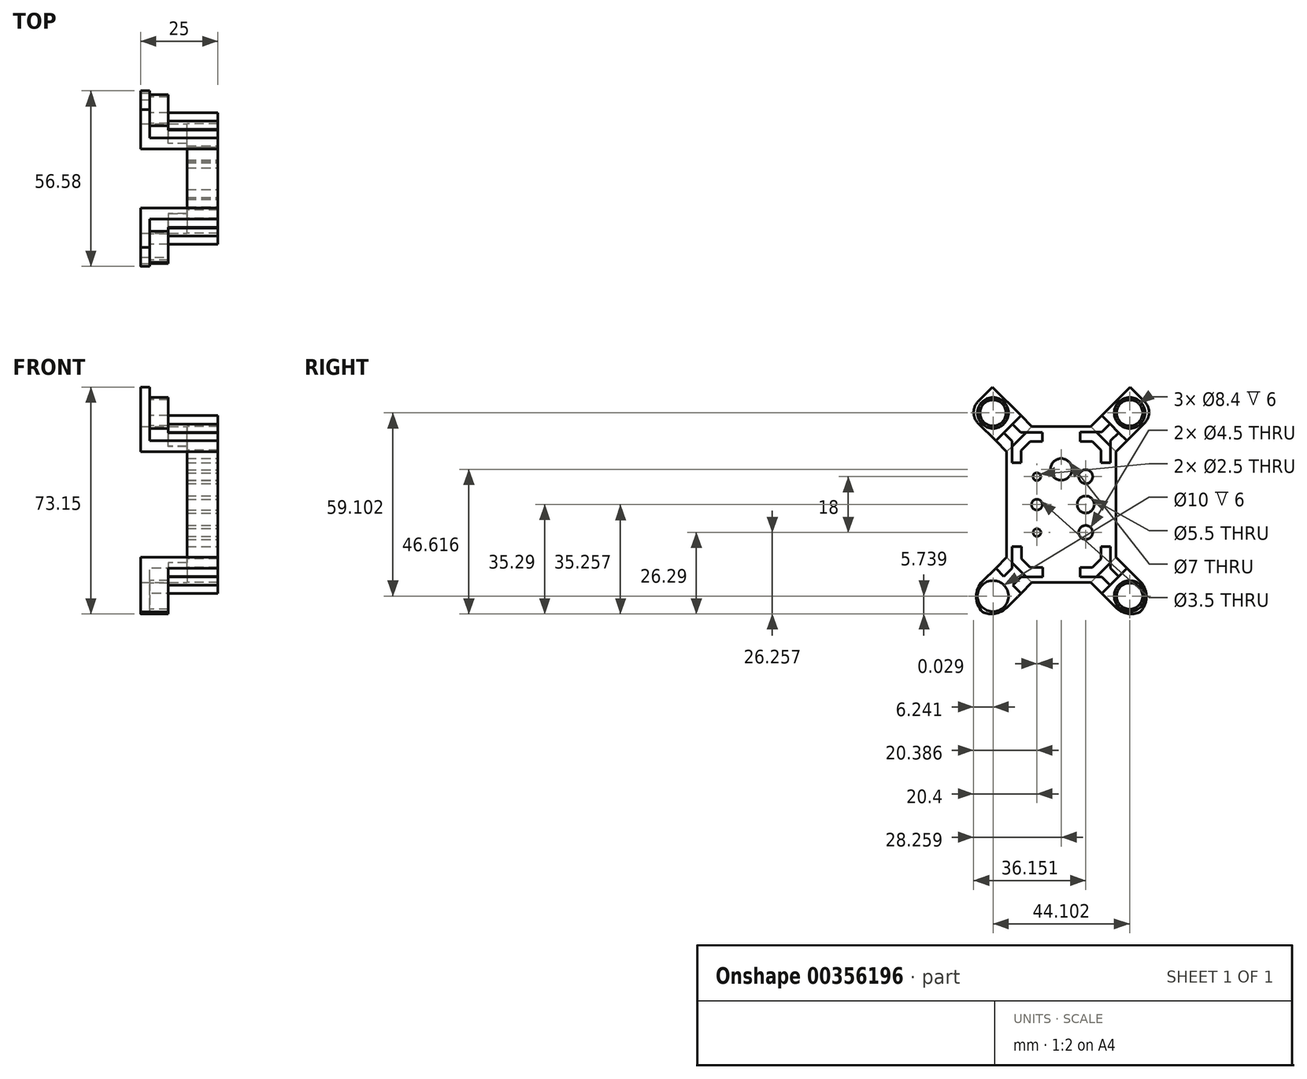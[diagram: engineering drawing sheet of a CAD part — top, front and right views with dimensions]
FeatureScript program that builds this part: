
annotation { "Feature Type Name" : "Feature", "Feature Type Description" : "" }
export const myFeature = defineFeature(function(context is Context, id is Id, definition is map)
    precondition{}
    {
        {
            var Q0;
            Q0=qCreatedBy(makeId("Right.planeOp"),FACE);
            var sketch = newSketch(context, id + "F0", { "sketchPlane" : qUnion([Q0])});
            skPoint(sketch, "E0", {"position": v(0, 42) * mm});
            skPoint(sketch, "E1", {"position": v(8.13, 50.13) * mm});
            skPoint(sketch, "E2", {"position": v(27.13, 50.13) * mm});
            skPoint(sketch, "E3", {"position": v(35.26, 42) * mm});
            skPoint(sketch, "E4", {"position": v(35.26, 8) * mm});
            skPoint(sketch, "E5", {"position": v(27.13, -0.13) * mm});
            skPoint(sketch, "E6", {"position": v(8.13, -0.13) * mm});
            skPoint(sketch, "E7", {"position": v(0, 8) * mm});
            skLineSegment(sketch, "E8", {"start": v(0, 42) * mm, "end": v(8.13, 50.13) * mm});
            skLineSegment(sketch, "E9", {"start": v(27.13, 50.13) * mm, "end": v(8.13, 50.13) * mm});
            skLineSegment(sketch, "E10", {"start": v(27.13, 50.13) * mm, "end": v(35.26, 42) * mm});
            skLineSegment(sketch, "E11", {"start": v(35.26, 8) * mm, "end": v(35.26, 42) * mm});
            skLineSegment(sketch, "E12", {"start": v(35.26, 8) * mm, "end": v(27.13, -0.13) * mm});
            skLineSegment(sketch, "E13", {"start": v(0, 8) * mm, "end": v(8.13, -0.13) * mm});
            skLineSegment(sketch, "E14", {"start": v(8.13, -0.13) * mm, "end": v(27.13, -0.13) * mm});
            skLineSegment(sketch, "E15", {"start": v(0, 8) * mm, "end": v(0, 42) * mm});
            skPoint(sketch, "E16", {"position": v(4.07, 46.07) * mm});
            skPoint(sketch, "E17", {"position": v(5.48, 47.48) * mm});
            skPoint(sketch, "E18", {"position": v(2.65, 44.65) * mm});
            skLineSegment(sketch, "E19", {"start": v(2.65, 44.65) * mm, "end": v(5, 42.3) * mm});
            skLineSegment(sketch, "E20", {"start": v(5.48, 47.48) * mm, "end": v(7.83, 45.13) * mm});
            skLineSegment(sketch, "E21", {"start": v(5.48, 47.48) * mm, "end": v(2.65, 44.65) * mm});
            skPoint(sketch, "E22", {"position": v(31.2, 46.07) * mm});
            skPoint(sketch, "E23", {"position": v(29.78, 47.48) * mm});
            skPoint(sketch, "E24", {"position": v(32.61, 44.65) * mm});
            skPoint(sketch, "E25", {"position": v(31.2, 3.93) * mm});
            skPoint(sketch, "E26", {"position": v(32.61, 5.35) * mm});
            skPoint(sketch, "E27", {"position": v(29.78, 2.52) * mm});
            skPoint(sketch, "E28", {"position": v(4.07, 3.93) * mm});
            skPoint(sketch, "E29", {"position": v(2.65, 5.35) * mm});
            skPoint(sketch, "E30", {"position": v(5.48, 2.52) * mm});
            skLineSegment(sketch, "E31", {"start": v(29.78, 47.48) * mm, "end": v(27.44, 45.13) * mm});
            skLineSegment(sketch, "E32", {"start": v(32.61, 44.65) * mm, "end": v(30.26, 42.3) * mm});
            skLineSegment(sketch, "E33", {"start": v(29.78, 2.52) * mm, "end": v(27.44, 4.87) * mm});
            skLineSegment(sketch, "E34", {"start": v(32.61, 5.35) * mm, "end": v(30.26, 7.7) * mm});
            skPoint(sketch, "E35", {"position": v(17.63, 50.13) * mm});
            skPoint(sketch, "E36", {"position": v(35.26, 25) * mm});
            skSolve(sketch);
        }
        {
            var Q0;
            {var subQ6=sQuery(id+"F0.wireOp",EDGE,"E9");Q0=makeQuery(id+"F0.imprint","IMPRINT",FACE,{"disambiguationData":[TD([[makeQuery(id+"F0.imprint","IMPRINT",EDGE,{"derivedFrom":subQ6}),1.0]])]});}
            extrude(context, id + "F1", {"entities" : qUnion([Q0]), "depth" : 10 * mm});
        }
        {
            var Q0;
            Q0=makeQuery(id+"F1.opExtrude","SWEPT_FACE",FACE,{"disambiguationData":[OSD([sQuery(id+"F0.wireOp",EDGE,"E12")])]});
            var sketch = newSketch(context, id + "F2", { "sketchPlane" : qUnion([Q0])});
            skPoint(sketch, "E37.oppositeSnap0", {"position": v(-5, 30.6) * mm});
            skLineSegment(sketch, "E37.bottom", {"start": v(-10, 19.1) * mm, "end": v(15, 19.1) * mm});
            skLineSegment(sketch, "E37.top", {"start": v(-10, 30.6) * mm, "end": v(15, 30.6) * mm});
            skLineSegment(sketch, "E37.left", {"start": v(-10, 19.1) * mm, "end": v(-10, 30.6) * mm});
            skLineSegment(sketch, "E37.right", {"start": v(15, 19.1) * mm, "end": v(15, 30.6) * mm});
            skSolve(sketch);
        }
        {
            var Q0;
            Q0 = qSketchRegion(id + "F2", true);
            extrude(context, id + "F3", {"entities" : qUnion([Q0]), "operationType" : NewBodyOperationType.ADD, "depth" : 5 * mm});
        }
        {
            var Q0;
            Q0=makeQuery(id+"F1.opExtrude","SWEPT_FACE",FACE,{"disambiguationData":[OSD([sQuery(id+"F0.wireOp",EDGE,"E10")])]});
            var sketch = newSketch(context, id + "F4", { "sketchPlane" : qUnion([Q0])});
            skLineSegment(sketch, "E38.bottom", {"start": v(-10, 4.76) * mm, "end": v(15, 4.76) * mm});
            skLineSegment(sketch, "E38.top", {"start": v(-10, 16.26) * mm, "end": v(15, 16.26) * mm});
            skLineSegment(sketch, "E38.left", {"start": v(-10, 4.76) * mm, "end": v(-10, 16.26) * mm});
            skLineSegment(sketch, "E38.right", {"start": v(15, 4.76) * mm, "end": v(15, 16.26) * mm});
            skSolve(sketch);
        }
        {
            var Q0;
            Q0 = qSketchRegion(id + "F4", true);
            extrude(context, id + "F5", {"entities" : qUnion([Q0]), "operationType" : NewBodyOperationType.ADD, "depth" : 5 * mm});
        }
        {
            var Q0;
            Q0=makeQuery(id+"F1.opExtrude","SWEPT_FACE",FACE,{"disambiguationData":[OSD([sQuery(id+"F0.wireOp",EDGE,"E13")])]});
            var sketch = newSketch(context, id + "F6", { "sketchPlane" : qUnion([Q0])});
            skPoint(sketch, "E39.oppositeSnap0", {"position": v(5, -5.84) * mm});
            skLineSegment(sketch, "E39.bottom", {"start": v(10, 5.66) * mm, "end": v(-15, 5.66) * mm});
            skLineSegment(sketch, "E39.top", {"start": v(10, -5.84) * mm, "end": v(-15, -5.84) * mm});
            skLineSegment(sketch, "E39.left", {"start": v(10, 5.66) * mm, "end": v(10, -5.84) * mm});
            skLineSegment(sketch, "E39.right", {"start": v(-15, 5.66) * mm, "end": v(-15, -5.84) * mm});
            skSolve(sketch);
        }
        {
            var Q0;
            Q0 = qSketchRegion(id + "F6", true);
            extrude(context, id + "F7", {"entities" : qUnion([Q0]), "operationType" : NewBodyOperationType.ADD, "depth" : 5 * mm});
        }
        {
            var Q0;
            Q0=makeQuery(id+"F1.opExtrude","SWEPT_FACE",FACE,{"disambiguationData":[OSD([sQuery(id+"F0.wireOp",EDGE,"E8")])]});
            var sketch = newSketch(context, id + "F8", { "sketchPlane" : qUnion([Q0])});
            skPoint(sketch, "E40.oppositeSnap0", {"position": v(5, 29.7) * mm});
            skLineSegment(sketch, "E40.bottom", {"start": v(10, 41.2) * mm, "end": v(-15, 41.2) * mm});
            skLineSegment(sketch, "E40.top", {"start": v(10, 29.7) * mm, "end": v(-15, 29.7) * mm});
            skLineSegment(sketch, "E40.left", {"start": v(10, 41.2) * mm, "end": v(10, 29.7) * mm});
            skLineSegment(sketch, "E40.right", {"start": v(-15, 41.2) * mm, "end": v(-15, 29.7) * mm});
            skSolve(sketch);
        }
        {
            var Q0;
            Q0 = qSketchRegion(id + "F8", true);
            extrude(context, id + "F9", {"entities" : qUnion([Q0]), "operationType" : NewBodyOperationType.ADD, "depth" : 5 * mm});
        }
        {
            var Q0;
            Q0=makeQuery(id+"F9.opExtrude","CAP_FACE",FACE,{"disambiguationData":[OSD([sQuery(id+"F8.wireOp",EDGE,"E40.bottom"),sQuery(id+"F8.wireOp",EDGE,"E40.top"),sQuery(id+"F8.wireOp",EDGE,"E40.left"),sQuery(id+"F8.wireOp",EDGE,"E40.right")])],"isStart":false});
            var sketch = newSketch(context, id + "F10", { "sketchPlane" : qUnion([Q0])});
            skPoint(sketch, "E41", {"position": v(10, 41.2) * mm});
            skPoint(sketch, "E42", {"position": v(10, 29.7) * mm});
            skPoint(sketch, "E43", {"position": v(10, 37.36) * mm});
            skPoint(sketch, "E44", {"position": v(10, 33.36) * mm});
            skLineSegment(sketch, "E45.bottom", {"start": v(10, 37.36) * mm, "end": v(-6, 37.36) * mm});
            skLineSegment(sketch, "E45.top", {"start": v(10, 33.36) * mm, "end": v(-6, 33.36) * mm});
            skLineSegment(sketch, "E45.left", {"start": v(10, 37.36) * mm, "end": v(10, 33.36) * mm});
            skLineSegment(sketch, "E45.right", {"start": v(-6, 37.36) * mm, "end": v(-6, 33.36) * mm});
            skSolve(sketch);
        }
        {
            var Q0;
            Q0 = qSketchRegion(id + "F10", true);
            extrude(context, id + "F11", {"entities" : qUnion([Q0]), "operationType" : NewBodyOperationType.REMOVE, "oppositeDirection" : true, "depth" : 8 * mm});
        }
        {
            var Q0;
            Q0=makeQuery(id+"F9.boolean.opBoolean","MERGE",FACE,{"derivedFrom":[makeQuery(id+"F7.boolean.opBoolean","MERGE",FACE,{"derivedFrom":[makeQuery(id+"F5.boolean.opBoolean","MERGE",FACE,{"derivedFrom":[makeQuery(id+"F3.boolean.opBoolean","MERGE",FACE,{"derivedFrom":[makeQuery(id+"F1.opExtrude","CAP_FACE",FACE,{"disambiguationData":[OSD([sQuery(id+"F0.wireOp",EDGE,"E8"),sQuery(id+"F0.wireOp",EDGE,"E9"),sQuery(id+"F0.wireOp",EDGE,"E10"),sQuery(id+"F0.wireOp",EDGE,"E11"),sQuery(id+"F0.wireOp",EDGE,"E12"),sQuery(id+"F0.wireOp",EDGE,"E13"),sQuery(id+"F0.wireOp",EDGE,"E14"),sQuery(id+"F0.wireOp",EDGE,"E15")])],"isStart":false}),makeQuery(id+"F3.opExtrude","SWEPT_FACE",FACE,{"disambiguationData":[OSD([sQuery(id+"F2.wireOp",EDGE,"E37.left")])]})]}),makeQuery(id+"F5.opExtrude","SWEPT_FACE",FACE,{"disambiguationData":[OSD([sQuery(id+"F4.wireOp",EDGE,"E38.left")])]})]}),makeQuery(id+"F7.opExtrude","SWEPT_FACE",FACE,{"disambiguationData":[OSD([sQuery(id+"F6.wireOp",EDGE,"E39.left")])]})]}),makeQuery(id+"F9.opExtrude","SWEPT_FACE",FACE,{"disambiguationData":[OSD([sQuery(id+"F8.wireOp",EDGE,"E40.left")])]})]});
            var sketch = newSketch(context, id + "F12", { "sketchPlane" : qUnion([Q0])});
            skLineSegment(sketch, "E46", {"start": v(4.7, 42.46) * mm, "end": v(4.7, 38.46) * mm});
            skLineSegment(sketch, "E47", {"start": v(4.7, 38.46) * mm, "end": v(1.7, 38.46) * mm});
            skLineSegment(sketch, "E48", {"start": v(1.7, 38.46) * mm, "end": v(1.7, 45.46) * mm});
            skLineSegment(sketch, "E49", {"start": v(7.54, 45.3) * mm, "end": v(11.54, 45.3) * mm});
            skLineSegment(sketch, "E50", {"start": v(11.54, 45.3) * mm, "end": v(11.54, 48.3) * mm});
            skLineSegment(sketch, "E51", {"start": v(11.54, 48.3) * mm, "end": v(4.54, 48.3) * mm});
            skSolve(sketch);
        }
        {
            var Q0;
            Q0=makeQuery(id+"F9.opExtrude","CAP_FACE",FACE,{"disambiguationData":[OSD([sQuery(id+"F8.wireOp",EDGE,"E40.bottom"),sQuery(id+"F8.wireOp",EDGE,"E40.top"),sQuery(id+"F8.wireOp",EDGE,"E40.left"),sQuery(id+"F8.wireOp",EDGE,"E40.right")])],"isStart":true});
            var sketch = newSketch(context, id + "F13", { "sketchPlane" : qUnion([Q0])});
            skLineSegment(sketch, "E52.bottom", {"start": v(0, 29.7) * mm, "end": v(15, 29.7) * mm});
            skLineSegment(sketch, "E52.top", {"start": v(0, 41.2) * mm, "end": v(15, 41.2) * mm});
            skLineSegment(sketch, "E52.left", {"start": v(0, 29.7) * mm, "end": v(0, 41.2) * mm});
            skLineSegment(sketch, "E52.right", {"start": v(15, 29.7) * mm, "end": v(15, 41.2) * mm});
            skSolve(sketch);
        }
        {
            var Q0;
            Q0 = qSketchRegion(id + "F13", true);
            extrude(context, id + "F14", {"entities" : qUnion([Q0]), "operationType" : NewBodyOperationType.ADD, "depth" : 7 * mm});
        }
        {
            var Q0;
            Q0 = qSketchRegion(id + "F12", true);
            var Q1;
            {var subQ0=sQuery(id+"F12.wireOp",EDGE,"E49");Q1=makeQuery(id+"F12.imprint","IMPRINT",FACE,{"disambiguationData":[TD([[makeQuery(id+"F12.imprint","IMPRINT",EDGE,{"derivedFrom":subQ0}),1.0]])]});}
            var Q2;
            {var subQ0=sQuery(id+"F12.wireOp",EDGE,"E46");Q2=makeQuery(id+"F12.imprint","IMPRINT",FACE,{"disambiguationData":[TD([[makeQuery(id+"F12.imprint","IMPRINT",EDGE,{"derivedFrom":subQ0}),-1.0]])]});}
            extrude(context, id + "F15", {"entities" : qUnion([Q0, Q1, Q2]), "operationType" : NewBodyOperationType.REMOVE, "oppositeDirection" : true, "depth" : 10 * mm});
        }
        {
            var Q0;
            Q0=makeQuery(id+"F5.opExtrude","CAP_FACE",FACE,{"disambiguationData":[OSD([sQuery(id+"F4.wireOp",EDGE,"E38.bottom"),sQuery(id+"F4.wireOp",EDGE,"E38.top"),sQuery(id+"F4.wireOp",EDGE,"E38.left"),sQuery(id+"F4.wireOp",EDGE,"E38.right")])],"isStart":false});
            var sketch = newSketch(context, id + "F16", { "sketchPlane" : qUnion([Q0])});
            skPoint(sketch, "E53", {"position": v(-10, 8.51) * mm});
            skPoint(sketch, "E54", {"position": v(-10, 12.51) * mm});
            skLineSegment(sketch, "E55.bottom", {"start": v(-10, 8.51) * mm, "end": v(6, 8.51) * mm});
            skLineSegment(sketch, "E55.top", {"start": v(-10, 12.51) * mm, "end": v(6, 12.51) * mm});
            skLineSegment(sketch, "E55.left", {"start": v(-10, 8.51) * mm, "end": v(-10, 12.51) * mm});
            skLineSegment(sketch, "E55.right", {"start": v(6, 8.51) * mm, "end": v(6, 12.51) * mm});
            skPoint(sketch, "E56", {"position": v(-10, 4.76) * mm});
            skPoint(sketch, "E57", {"position": v(-10, 16.26) * mm});
            skSolve(sketch);
        }
        {
            var Q0;
            Q0 = qSketchRegion(id + "F16", true);
            extrude(context, id + "F17", {"entities" : qUnion([Q0]), "operationType" : NewBodyOperationType.REMOVE, "oppositeDirection" : true, "depth" : 8 * mm});
        }
        {
            var Q0;
            Q0=makeQuery(id+"F5.opExtrude","CAP_FACE",FACE,{"disambiguationData":[OSD([sQuery(id+"F4.wireOp",EDGE,"E38.bottom"),sQuery(id+"F4.wireOp",EDGE,"E38.top"),sQuery(id+"F4.wireOp",EDGE,"E38.left"),sQuery(id+"F4.wireOp",EDGE,"E38.right")])],"isStart":true});
            var sketch = newSketch(context, id + "F18", { "sketchPlane" : qUnion([Q0])});
            skLineSegment(sketch, "E58.bottom", {"start": v(0, 16.26) * mm, "end": v(-15, 16.26) * mm});
            skLineSegment(sketch, "E58.top", {"start": v(0, 4.76) * mm, "end": v(-15, 4.76) * mm});
            skLineSegment(sketch, "E58.left", {"start": v(0, 16.26) * mm, "end": v(0, 4.76) * mm});
            skLineSegment(sketch, "E58.right", {"start": v(-15, 16.26) * mm, "end": v(-15, 4.76) * mm});
            skSolve(sketch);
        }
        {
            var Q0;
            Q0 = qSketchRegion(id + "F18", true);
            extrude(context, id + "F19", {"entities" : qUnion([Q0]), "operationType" : NewBodyOperationType.ADD, "depth" : 7 * mm});
        }
        {
            var Q0;
            Q0=makeQuery(id+"F3.opExtrude","CAP_FACE",FACE,{"disambiguationData":[OSD([sQuery(id+"F2.wireOp",EDGE,"E37.bottom"),sQuery(id+"F2.wireOp",EDGE,"E37.top"),sQuery(id+"F2.wireOp",EDGE,"E37.left"),sQuery(id+"F2.wireOp",EDGE,"E37.right")])],"isStart":false});
            var sketch = newSketch(context, id + "F20", { "sketchPlane" : qUnion([Q0])});
            skPoint(sketch, "E59", {"position": v(-10, 22.84) * mm});
            skPoint(sketch, "E60", {"position": v(-10, 26.84) * mm});
            skLineSegment(sketch, "E61.bottom", {"start": v(-10, 22.84) * mm, "end": v(6, 22.84) * mm});
            skLineSegment(sketch, "E61.top", {"start": v(-10, 26.84) * mm, "end": v(6, 26.84) * mm});
            skLineSegment(sketch, "E61.left", {"start": v(-10, 22.84) * mm, "end": v(-10, 26.84) * mm});
            skLineSegment(sketch, "E61.right", {"start": v(6, 22.84) * mm, "end": v(6, 26.84) * mm});
            skSolve(sketch);
        }
        {
            var Q0;
            Q0 = qSketchRegion(id + "F20", true);
            extrude(context, id + "F21", {"entities" : qUnion([Q0]), "operationType" : NewBodyOperationType.REMOVE, "oppositeDirection" : true, "depth" : 8 * mm});
        }
        {
            var Q0;
            Q0=makeQuery(id+"F7.opExtrude","CAP_FACE",FACE,{"disambiguationData":[OSD([sQuery(id+"F6.wireOp",EDGE,"E39.bottom"),sQuery(id+"F6.wireOp",EDGE,"E39.top"),sQuery(id+"F6.wireOp",EDGE,"E39.left"),sQuery(id+"F6.wireOp",EDGE,"E39.right")])],"isStart":false});
            var sketch = newSketch(context, id + "F22", { "sketchPlane" : qUnion([Q0])});
            skPoint(sketch, "E62", {"position": v(10, 1.9) * mm});
            skPoint(sketch, "E63", {"position": v(10, -2.1) * mm});
            skLineSegment(sketch, "E64.bottom", {"start": v(10, 1.9) * mm, "end": v(-6, 1.9) * mm});
            skLineSegment(sketch, "E64.top", {"start": v(10, -2.1) * mm, "end": v(-6, -2.1) * mm});
            skLineSegment(sketch, "E64.left", {"start": v(10, 1.9) * mm, "end": v(10, -2.1) * mm});
            skLineSegment(sketch, "E64.right", {"start": v(-6, 1.9) * mm, "end": v(-6, -2.1) * mm});
            skSolve(sketch);
        }
        {
            var Q0;
            Q0 = qSketchRegion(id + "F22", true);
            extrude(context, id + "F23", {"entities" : qUnion([Q0]), "operationType" : NewBodyOperationType.REMOVE, "oppositeDirection" : true, "depth" : 8 * mm});
        }
        {
            var Q0;
            Q0=makeQuery(id+"F9.boolean.opBoolean","MERGE",FACE,{"derivedFrom":[makeQuery(id+"F7.boolean.opBoolean","MERGE",FACE,{"derivedFrom":[makeQuery(id+"F5.boolean.opBoolean","MERGE",FACE,{"derivedFrom":[makeQuery(id+"F3.boolean.opBoolean","MERGE",FACE,{"derivedFrom":[makeQuery(id+"F1.opExtrude","CAP_FACE",FACE,{"disambiguationData":[OSD([sQuery(id+"F0.wireOp",EDGE,"E8"),sQuery(id+"F0.wireOp",EDGE,"E9"),sQuery(id+"F0.wireOp",EDGE,"E10"),sQuery(id+"F0.wireOp",EDGE,"E11"),sQuery(id+"F0.wireOp",EDGE,"E12"),sQuery(id+"F0.wireOp",EDGE,"E13"),sQuery(id+"F0.wireOp",EDGE,"E14"),sQuery(id+"F0.wireOp",EDGE,"E15")])],"isStart":false}),makeQuery(id+"F3.opExtrude","SWEPT_FACE",FACE,{"disambiguationData":[OSD([sQuery(id+"F2.wireOp",EDGE,"E37.left")])]})]}),makeQuery(id+"F5.opExtrude","SWEPT_FACE",FACE,{"disambiguationData":[OSD([sQuery(id+"F4.wireOp",EDGE,"E38.left")])]})]}),makeQuery(id+"F7.opExtrude","SWEPT_FACE",FACE,{"disambiguationData":[OSD([sQuery(id+"F6.wireOp",EDGE,"E39.left")])]})]}),makeQuery(id+"F9.opExtrude","SWEPT_FACE",FACE,{"disambiguationData":[OSD([sQuery(id+"F8.wireOp",EDGE,"E40.left")])]})]});
            var sketch = newSketch(context, id + "F24", { "sketchPlane" : qUnion([Q0])});
            skLineSegment(sketch, "E65", {"start": v(7.6, 4.64) * mm, "end": v(11.6, 4.64) * mm});
            skLineSegment(sketch, "E66", {"start": v(11.6, 4.64) * mm, "end": v(11.6, 1.64) * mm});
            skLineSegment(sketch, "E67", {"start": v(11.6, 1.64) * mm, "end": v(4.6, 1.64) * mm});
            skLineSegment(sketch, "E68", {"start": v(4.77, 7.47) * mm, "end": v(4.77, 11.47) * mm});
            skLineSegment(sketch, "E69", {"start": v(4.77, 11.47) * mm, "end": v(1.77, 11.47) * mm});
            skLineSegment(sketch, "E70", {"start": v(1.77, 11.47) * mm, "end": v(1.77, 4.47) * mm});
            skLineSegment(sketch, "E71", {"start": v(27.66, 4.64) * mm, "end": v(23.66, 4.64) * mm});
            skLineSegment(sketch, "E72", {"start": v(23.66, 4.64) * mm, "end": v(23.66, 1.64) * mm});
            skLineSegment(sketch, "E73", {"start": v(23.66, 1.64) * mm, "end": v(30.66, 1.64) * mm});
            skLineSegment(sketch, "E74", {"start": v(30.5, 7.47) * mm, "end": v(30.5, 11.47) * mm});
            skLineSegment(sketch, "E75", {"start": v(30.5, 11.47) * mm, "end": v(33.5, 11.47) * mm});
            skLineSegment(sketch, "E76", {"start": v(33.5, 11.47) * mm, "end": v(33.5, 4.47) * mm});
            skLineSegment(sketch, "E77", {"start": v(30.5, 42.53) * mm, "end": v(30.5, 38.53) * mm});
            skLineSegment(sketch, "E78", {"start": v(30.5, 38.53) * mm, "end": v(33.5, 38.53) * mm});
            skLineSegment(sketch, "E79", {"start": v(33.5, 38.53) * mm, "end": v(33.5, 45.53) * mm});
            skLineSegment(sketch, "E80", {"start": v(27.66, 45.36) * mm, "end": v(23.66, 45.36) * mm});
            skLineSegment(sketch, "E81", {"start": v(23.66, 45.36) * mm, "end": v(23.66, 48.36) * mm});
            skLineSegment(sketch, "E82", {"start": v(23.66, 48.36) * mm, "end": v(30.66, 48.36) * mm});
            skSolve(sketch);
        }
        {
            var Q0;
            Q0=makeQuery(id+"F7.opExtrude","CAP_FACE",FACE,{"disambiguationData":[OSD([sQuery(id+"F6.wireOp",EDGE,"E39.bottom"),sQuery(id+"F6.wireOp",EDGE,"E39.top"),sQuery(id+"F6.wireOp",EDGE,"E39.left"),sQuery(id+"F6.wireOp",EDGE,"E39.right")])],"isStart":true});
            var sketch = newSketch(context, id + "F25", { "sketchPlane" : qUnion([Q0])});
            skLineSegment(sketch, "E83.bottom", {"start": v(0, -5.84) * mm, "end": v(15, -5.84) * mm});
            skLineSegment(sketch, "E83.top", {"start": v(0, 5.66) * mm, "end": v(15, 5.66) * mm});
            skLineSegment(sketch, "E83.left", {"start": v(0, -5.84) * mm, "end": v(0, 5.66) * mm});
            skLineSegment(sketch, "E83.right", {"start": v(15, -5.84) * mm, "end": v(15, 5.66) * mm});
            skSolve(sketch);
        }
        {
            var Q0;
            Q0 = qSketchRegion(id + "F25", true);
            extrude(context, id + "F26", {"entities" : qUnion([Q0]), "operationType" : NewBodyOperationType.ADD, "depth" : 8 * mm});
        }
        {
            var Q0;
            Q0=makeQuery(id+"F3.opExtrude","CAP_FACE",FACE,{"disambiguationData":[OSD([sQuery(id+"F2.wireOp",EDGE,"E37.bottom"),sQuery(id+"F2.wireOp",EDGE,"E37.top"),sQuery(id+"F2.wireOp",EDGE,"E37.left"),sQuery(id+"F2.wireOp",EDGE,"E37.right")])],"isStart":true});
            var sketch = newSketch(context, id + "F27", { "sketchPlane" : qUnion([Q0])});
            skLineSegment(sketch, "E84.bottom", {"start": v(0, 30.6) * mm, "end": v(-15, 30.6) * mm});
            skLineSegment(sketch, "E84.top", {"start": v(0, 19.1) * mm, "end": v(-15, 19.1) * mm});
            skLineSegment(sketch, "E84.left", {"start": v(0, 30.6) * mm, "end": v(0, 19.1) * mm});
            skLineSegment(sketch, "E84.right", {"start": v(-15, 30.6) * mm, "end": v(-15, 19.1) * mm});
            skSolve(sketch);
        }
        {
            var Q0;
            Q0 = qSketchRegion(id + "F27", true);
            extrude(context, id + "F28", {"entities" : qUnion([Q0]), "operationType" : NewBodyOperationType.ADD, "depth" : 8 * mm});
        }
        {
            var Q0;
            {var subQ0=sQuery(id+"F24.wireOp",EDGE,"E74");Q0=makeQuery(id+"F24.imprint","IMPRINT",FACE,{"disambiguationData":[TD([[makeQuery(id+"F24.imprint","IMPRINT",EDGE,{"derivedFrom":subQ0}),-1.0]])]});}
            var Q1;
            {var subQ0=sQuery(id+"F24.wireOp",EDGE,"E71");Q1=makeQuery(id+"F24.imprint","IMPRINT",FACE,{"disambiguationData":[TD([[makeQuery(id+"F24.imprint","IMPRINT",EDGE,{"derivedFrom":subQ0}),1.0]])]});}
            var Q2;
            {var subQ0=sQuery(id+"F24.wireOp",EDGE,"E68");Q2=makeQuery(id+"F24.imprint","IMPRINT",FACE,{"disambiguationData":[TD([[makeQuery(id+"F24.imprint","IMPRINT",EDGE,{"derivedFrom":subQ0}),1.0]])]});}
            var Q3;
            {var subQ0=sQuery(id+"F24.wireOp",EDGE,"E65");Q3=makeQuery(id+"F24.imprint","IMPRINT",FACE,{"disambiguationData":[TD([[makeQuery(id+"F24.imprint","IMPRINT",EDGE,{"derivedFrom":subQ0}),-1.0]])]});}
            var Q4;
            {var subQ0=sQuery(id+"F24.wireOp",EDGE,"E77");Q4=makeQuery(id+"F24.imprint","IMPRINT",FACE,{"disambiguationData":[TD([[makeQuery(id+"F24.imprint","IMPRINT",EDGE,{"derivedFrom":subQ0}),1.0]])]});}
            var Q5;
            {var subQ0=sQuery(id+"F24.wireOp",EDGE,"E80");Q5=makeQuery(id+"F24.imprint","IMPRINT",FACE,{"disambiguationData":[TD([[makeQuery(id+"F24.imprint","IMPRINT",EDGE,{"derivedFrom":subQ0}),-1.0]])]});}
            extrude(context, id + "F29", {"entities" : qUnion([Q0, Q1, Q2, Q3, Q4, Q5]), "operationType" : NewBodyOperationType.REMOVE, "oppositeDirection" : true, "depth" : 10 * mm});
        }
        {
            var Q0;
            Q0=makeQuery(id+"F28.opExtrude","SWEPT_FACE",FACE,{"disambiguationData":[OSD([sQuery(id+"F27.wireOp",EDGE,"E84.left")])]});
            extrude(context, id + "F30", {"entities" : qUnion([Q0]), "operationType" : NewBodyOperationType.REMOVE, "oppositeDirection" : true, "depth" : 6 * mm});
        }
        {
            var Q0;
            Q0=makeQuery(id+"F19.opExtrude","SWEPT_FACE",FACE,{"disambiguationData":[OSD([sQuery(id+"F18.wireOp",EDGE,"E58.left")])]});
            extrude(context, id + "F31", {"entities" : qUnion([Q0]), "operationType" : NewBodyOperationType.REMOVE, "oppositeDirection" : true, "depth" : 6 * mm});
        }
        {
            var Q0;
            Q0=makeQuery(id+"F14.opExtrude","SWEPT_FACE",FACE,{"disambiguationData":[OSD([sQuery(id+"F13.wireOp",EDGE,"E52.left")])]});
            extrude(context, id + "F32", {"entities" : qUnion([Q0]), "operationType" : NewBodyOperationType.REMOVE, "oppositeDirection" : true, "depth" : 6 * mm});
        }
        {
            var Q0;
            Q0=makeQuery(id+"F26.opExtrude","SWEPT_FACE",FACE,{"disambiguationData":[OSD([sQuery(id+"F25.wireOp",EDGE,"E83.left")])]});
            extrude(context, id + "F33", {"entities" : qUnion([Q0]), "operationType" : NewBodyOperationType.REMOVE, "oppositeDirection" : true, "depth" : 6 * mm});
        }
        {
            var Q0;
            {var subQ6=sQuery(id+"F0.wireOp",EDGE,"E9");Q0=makeQuery(id+"F0.imprint","IMPRINT",FACE,{"disambiguationData":[TD([[makeQuery(id+"F0.imprint","IMPRINT",EDGE,{"derivedFrom":subQ6}),1.0]])]});}
            extrude(context, id + "F34", {"entities" : qUnion([Q0]), "operationType" : NewBodyOperationType.REMOVE, "oppositeDirection" : true, "depth" : 25 * mm});
        }
        {
            var Q0;
            Q0=makeQuery(id+"F34.boolean.opBoolean","COPY",FACE,{"derivedFrom":makeQuery(id+"F34.opExtrude","SWEPT_FACE",FACE,{"disambiguationData":[OSD([sQuery(id+"F0.wireOp",EDGE,"E10")])]})});
            var sketch = newSketch(context, id + "F35", { "sketchPlane" : qUnion([Q0])});
            skPoint(sketch, "E85", {"position": v(-15, 10.51) * mm});
            skPoint(sketch, "E86", {"position": v(-15, 16.26) * mm});
            skPoint(sketch, "E87", {"position": v(-15, 4.76) * mm});
            skLineSegment(sketch, "E88.bottom", {"start": v(-15, 16.26) * mm, "end": v(-12, 16.26) * mm});
            skLineSegment(sketch, "E88.top", {"start": v(-15, 4.76) * mm, "end": v(-12, 4.76) * mm});
            skLineSegment(sketch, "E88.left", {"start": v(-15, 16.26) * mm, "end": v(-15, 4.76) * mm});
            skLineSegment(sketch, "E88.right", {"start": v(-12, 16.26) * mm, "end": v(-12, 4.76) * mm});
            skSolve(sketch);
        }
        {
            var Q0;
            Q0 = qSketchRegion(id + "F35", true);
            extrude(context, id + "F36", {"entities" : qUnion([Q0]), "operationType" : NewBodyOperationType.ADD, "oppositeDirection" : true, "depth" : 18 * mm});
        }
        {
            var Q0;
            Q0=makeQuery(id+"F36.opExtrude","SWEPT_FACE",FACE,{"disambiguationData":[OSD([sQuery(id+"F35.wireOp",EDGE,"E88.right")])]});
            var sketch = newSketch(context, id + "F37", { "sketchPlane" : qUnion([Q0])});
            skPoint(sketch, "E89", {"position": v(43.93, 58.8) * mm});
            skPoint(sketch, "E90", {"position": v(35.62, 58.62) * mm});
            skPoint(sketch, "E91", {"position": v(43.75, 50.49) * mm});
            skLineSegment(sketch, "E92", {"start": v(43.75, 50.49) * mm, "end": v(35.62, 58.62) * mm});
            skPoint(sketch, "E93", {"position": v(39.68, 54.55) * mm});
            skCircle(sketch, "E94", {"center": v(39.68, 54.55) * mm, "radius": 5 * mm});
            skCircle(sketch, "E95", {"center": v(39.68, 54.55) * mm, "radius": 4.2 * mm});
            skSolve(sketch);
        }
        {
            var Q0;
            {var subQ0=sQuery(id+"F37.wireOp",EDGE,"E94");var subQ1=sQuery(id+"F37.wireOp",EDGE,"E92");var subQ2=makeQuery(id+"F37.imprint","INTERSECT",VERTEX,{"disambiguationData":[OD(0.0)],"derivedFrom":[subQ1,subQ0]});Q0=makeQuery(id+"F37.imprint","IMPRINT",FACE,{"disambiguationData":[TD([[makeQuery(id+"F37.imprint","IMPRINT",EDGE,{"disambiguationData":[TD([[subQ2,-1.0]])],"derivedFrom":subQ1}),1.0]])]});}
            var Q1;
            {var subQ0=sQuery(id+"F37.wireOp",EDGE,"E94");var subQ1=sQuery(id+"F37.wireOp",EDGE,"E92");var subQ2=makeQuery(id+"F37.imprint","INTERSECT",VERTEX,{"disambiguationData":[OD(0.0)],"derivedFrom":[subQ1,subQ0]});Q1=makeQuery(id+"F37.imprint","IMPRINT",FACE,{"disambiguationData":[TD([[makeQuery(id+"F37.imprint","IMPRINT",EDGE,{"disambiguationData":[TD([[subQ2,-1.0]])],"derivedFrom":subQ1}),-1.0]])]});}
            extrude(context, id + "F38", {"entities" : qUnion([Q0, Q1]), "operationType" : NewBodyOperationType.ADD, "depth" : 6 * mm});
        }
        {
            var Q0;
            Q0=makeQuery(id+"F34.boolean.opBoolean","COPY",FACE,{"derivedFrom":makeQuery(id+"F34.opExtrude","SWEPT_FACE",FACE,{"disambiguationData":[OSD([sQuery(id+"F0.wireOp",EDGE,"E8")])]})});
            var sketch = newSketch(context, id + "F39", { "sketchPlane" : qUnion([Q0])});
            skLineSegment(sketch, "E96.bottom", {"start": v(15, 29.7) * mm, "end": v(12, 29.7) * mm});
            skLineSegment(sketch, "E96.top", {"start": v(15, 41.2) * mm, "end": v(12, 41.2) * mm});
            skLineSegment(sketch, "E96.left", {"start": v(15, 29.7) * mm, "end": v(15, 41.2) * mm});
            skLineSegment(sketch, "E96.right", {"start": v(12, 29.7) * mm, "end": v(12, 41.2) * mm});
            skSolve(sketch);
        }
        {
            var Q0;
            Q0 = qSketchRegion(id + "F39", true);
            extrude(context, id + "F40", {"entities" : qUnion([Q0]), "operationType" : NewBodyOperationType.ADD, "oppositeDirection" : true, "depth" : 18 * mm});
        }
        {
            var Q0;
            Q0=makeQuery(id+"F40.opExtrude","SWEPT_FACE",FACE,{"disambiguationData":[OSD([sQuery(id+"F39.wireOp",EDGE,"E96.right")])]});
            var sketch = newSketch(context, id + "F41", { "sketchPlane" : qUnion([Q0])});
            skPoint(sketch, "E97", {"position": v(-8.66, 58.8) * mm});
            skPoint(sketch, "E98", {"position": v(-8.49, 50.49) * mm});
            skPoint(sketch, "E99", {"position": v(-0.35, 58.62) * mm});
            skLineSegment(sketch, "E100", {"start": v(-0.35, 58.62) * mm, "end": v(-8.49, 50.49) * mm});
            skPoint(sketch, "E101", {"position": v(-4.42, 54.55) * mm});
            skCircle(sketch, "E102", {"center": v(-4.42, 54.55) * mm, "radius": 5 * mm});
            skCircle(sketch, "E103", {"center": v(-4.42, 54.55) * mm, "radius": 4.2 * mm});
            skSolve(sketch);
        }
        {
            var Q0;
            {var subQ0=sQuery(id+"F41.wireOp",EDGE,"E102");var subQ1=sQuery(id+"F41.wireOp",EDGE,"E100");var subQ2=makeQuery(id+"F41.imprint","INTERSECT",VERTEX,{"disambiguationData":[OD(0.0)],"derivedFrom":[subQ1,subQ0]});Q0=makeQuery(id+"F41.imprint","IMPRINT",FACE,{"disambiguationData":[TD([[makeQuery(id+"F41.imprint","IMPRINT",EDGE,{"disambiguationData":[TD([[subQ2,-1.0]])],"derivedFrom":subQ1}),-1.0]])]});}
            var Q1;
            {var subQ0=sQuery(id+"F41.wireOp",EDGE,"E102");var subQ1=sQuery(id+"F41.wireOp",EDGE,"E100");var subQ2=makeQuery(id+"F41.imprint","INTERSECT",VERTEX,{"disambiguationData":[OD(0.0)],"derivedFrom":[subQ1,subQ0]});Q1=makeQuery(id+"F41.imprint","IMPRINT",FACE,{"disambiguationData":[TD([[makeQuery(id+"F41.imprint","IMPRINT",EDGE,{"disambiguationData":[TD([[subQ2,-1.0]])],"derivedFrom":subQ1}),1.0]])]});}
            extrude(context, id + "F42", {"entities" : qUnion([Q0, Q1]), "operationType" : NewBodyOperationType.ADD, "depth" : 6 * mm});
        }
        {
            var Q0;
            Q0=makeQuery(id+"F40.opExtrude","CAP_EDGE",EDGE,{"disambiguationData":[OSD([sQuery(id+"F39.wireOp",EDGE,"E96.bottom")])],"isStart":false});
            fillet(context, id + "F43", {"entities" : qUnion([Q0]), "radius" : 5 * mm, "tangentPropagation" : true, "allowEdgeOverflow" : false});
        }
        {
            var Q0;
            Q0=makeQuery(id+"F36.opExtrude","CAP_EDGE",EDGE,{"disambiguationData":[OSD([sQuery(id+"F35.wireOp",EDGE,"E88.top")])],"isStart":false});
            fillet(context, id + "F44", {"entities" : qUnion([Q0]), "radius" : 5 * mm, "tangentPropagation" : true, "allowEdgeOverflow" : false});
        }
        {
            var Q0;
            Q0=makeQuery(id+"F34.boolean.opBoolean","COPY",FACE,{"derivedFrom":makeQuery(id+"F34.opExtrude","SWEPT_FACE",FACE,{"disambiguationData":[OSD([sQuery(id+"F0.wireOp",EDGE,"E12")])]})});
            var sketch = newSketch(context, id + "F45", { "sketchPlane" : qUnion([Q0])});
            skLineSegment(sketch, "E104.bottom", {"start": v(-15, 30.6) * mm, "end": v(-12, 30.6) * mm});
            skLineSegment(sketch, "E104.top", {"start": v(-15, 19.1) * mm, "end": v(-12, 19.1) * mm});
            skLineSegment(sketch, "E104.left", {"start": v(-15, 30.6) * mm, "end": v(-15, 19.1) * mm});
            skLineSegment(sketch, "E104.right", {"start": v(-12, 30.6) * mm, "end": v(-12, 19.1) * mm});
            skSolve(sketch);
        }
        {
            var Q0;
            Q0 = qSketchRegion(id + "F45", true);
            extrude(context, id + "F46", {"entities" : qUnion([Q0]), "operationType" : NewBodyOperationType.ADD, "oppositeDirection" : true, "depth" : 18 * mm});
        }
        {
            var Q0;
            Q0=makeQuery(id+"F46.opExtrude","SWEPT_FACE",FACE,{"disambiguationData":[OSD([sQuery(id+"F45.wireOp",EDGE,"E104.right")])]});
            var sketch = newSketch(context, id + "F47", { "sketchPlane" : qUnion([Q0])});
            skPoint(sketch, "E105", {"position": v(35.62, -8.62) * mm});
            skPoint(sketch, "E106", {"position": v(43.75, -0.49) * mm});
            skLineSegment(sketch, "E107", {"start": v(43.75, -0.49) * mm, "end": v(35.62, -8.62) * mm});
            skCircle(sketch, "E108", {"center": v(39.68, -4.55) * mm, "radius": 5 * mm});
            skCircle(sketch, "E109", {"center": v(39.68, -4.55) * mm, "radius": 4.2 * mm});
            skSolve(sketch);
        }
        {
            var Q0;
            {var subQ0=sQuery(id+"F47.wireOp",EDGE,"E108");var subQ1=sQuery(id+"F47.wireOp",EDGE,"E107");var subQ2=makeQuery(id+"F47.imprint","INTERSECT",VERTEX,{"disambiguationData":[OD(0.0)],"derivedFrom":[subQ1,subQ0]});Q0=makeQuery(id+"F47.imprint","IMPRINT",FACE,{"disambiguationData":[TD([[makeQuery(id+"F47.imprint","IMPRINT",EDGE,{"disambiguationData":[TD([[subQ2,-1.0]])],"derivedFrom":subQ1}),-1.0]])]});}
            var Q1;
            {var subQ0=sQuery(id+"F47.wireOp",EDGE,"E108");var subQ1=sQuery(id+"F47.wireOp",EDGE,"E107");var subQ2=makeQuery(id+"F47.imprint","INTERSECT",VERTEX,{"disambiguationData":[OD(0.0)],"derivedFrom":[subQ1,subQ0]});Q1=makeQuery(id+"F47.imprint","IMPRINT",FACE,{"disambiguationData":[TD([[makeQuery(id+"F47.imprint","IMPRINT",EDGE,{"disambiguationData":[TD([[subQ2,-1.0]])],"derivedFrom":subQ1}),1.0]])]});}
            extrude(context, id + "F48", {"entities" : qUnion([Q0, Q1]), "operationType" : NewBodyOperationType.ADD, "depth" : 6 * mm});
        }
        {
            var Q0;
            Q0=makeQuery(id+"F34.boolean.opBoolean","COPY",FACE,{"derivedFrom":makeQuery(id+"F34.opExtrude","SWEPT_FACE",FACE,{"disambiguationData":[OSD([sQuery(id+"F0.wireOp",EDGE,"E13")])]})});
            var sketch = newSketch(context, id + "F49", { "sketchPlane" : qUnion([Q0])});
            skLineSegment(sketch, "E110.bottom", {"start": v(15, -5.84) * mm, "end": v(12, -5.84) * mm});
            skLineSegment(sketch, "E110.top", {"start": v(15, 5.66) * mm, "end": v(12, 5.66) * mm});
            skLineSegment(sketch, "E110.left", {"start": v(15, -5.84) * mm, "end": v(15, 5.66) * mm});
            skLineSegment(sketch, "E110.right", {"start": v(12, -5.84) * mm, "end": v(12, 5.66) * mm});
            skSolve(sketch);
        }
        {
            var Q0;
            Q0 = qSketchRegion(id + "F49", true);
            extrude(context, id + "F50", {"entities" : qUnion([Q0]), "operationType" : NewBodyOperationType.ADD, "oppositeDirection" : true, "depth" : 18 * mm});
        }
        {
            var Q0;
            Q0=makeQuery(id+"F50.opExtrude","SWEPT_FACE",FACE,{"disambiguationData":[OSD([sQuery(id+"F49.wireOp",EDGE,"E110.right")])]});
            var sketch = newSketch(context, id + "F51", { "sketchPlane" : qUnion([Q0])});
            skPoint(sketch, "E111", {"position": v(-8.49, -0.49) * mm});
            skPoint(sketch, "E112", {"position": v(-0.35, -8.62) * mm});
            skLineSegment(sketch, "E113", {"start": v(-0.35, -8.62) * mm, "end": v(-8.49, -0.49) * mm});
            skCircle(sketch, "E114", {"center": v(-4.42, -4.55) * mm, "radius": 5 * mm});
            skCircle(sketch, "E115", {"center": v(-4.42, -4.73) * mm, "radius": 4.2 * mm});
            skSolve(sketch);
        }
        {
            var Q0;
            {var subQ0=sQuery(id+"F51.wireOp",EDGE,"E114");var subQ1=sQuery(id+"F51.wireOp",EDGE,"E113");var subQ2=makeQuery(id+"F51.imprint","INTERSECT",VERTEX,{"disambiguationData":[OD(0.0)],"derivedFrom":[subQ1,subQ0]});Q0=makeQuery(id+"F51.imprint","IMPRINT",FACE,{"disambiguationData":[TD([[makeQuery(id+"F51.imprint","IMPRINT",EDGE,{"disambiguationData":[TD([[subQ2,-1.0]])],"derivedFrom":subQ1}),-1.0]])]});}
            var Q1;
            {var subQ0=sQuery(id+"F51.wireOp",EDGE,"E114");var subQ1=sQuery(id+"F51.wireOp",EDGE,"E113");var subQ2=makeQuery(id+"F51.imprint","INTERSECT",VERTEX,{"disambiguationData":[OD(0.0)],"derivedFrom":[subQ1,subQ0]});Q1=makeQuery(id+"F51.imprint","IMPRINT",FACE,{"disambiguationData":[TD([[makeQuery(id+"F51.imprint","IMPRINT",EDGE,{"disambiguationData":[TD([[subQ2,-1.0]])],"derivedFrom":subQ1}),1.0]])]});}
            extrude(context, id + "F52", {"entities" : qUnion([Q0, Q1]), "operationType" : NewBodyOperationType.ADD, "depth" : 6 * mm});
        }
        {
            var Q0;
            Q0=makeQuery(id+"F50.opExtrude","CAP_EDGE",EDGE,{"disambiguationData":[OSD([sQuery(id+"F49.wireOp",EDGE,"E110.top")])],"isStart":false});
            var Q1;
            Q1=makeQuery(id+"F46.opExtrude","CAP_EDGE",EDGE,{"disambiguationData":[OSD([sQuery(id+"F45.wireOp",EDGE,"E104.bottom")])],"isStart":false});
            fillet(context, id + "F53", {"entities" : qUnion([Q0, Q1]), "radius" : 7 * mm, "tangentPropagation" : true, "allowEdgeOverflow" : false});
        }
        {
            var Q0;
            Q0=makeQuery(id+"F9.boolean.opBoolean","MERGE",FACE,{"derivedFrom":[makeQuery(id+"F7.boolean.opBoolean","MERGE",FACE,{"derivedFrom":[makeQuery(id+"F5.boolean.opBoolean","MERGE",FACE,{"derivedFrom":[makeQuery(id+"F3.boolean.opBoolean","MERGE",FACE,{"derivedFrom":[makeQuery(id+"F1.opExtrude","CAP_FACE",FACE,{"disambiguationData":[OSD([sQuery(id+"F0.wireOp",EDGE,"E8"),sQuery(id+"F0.wireOp",EDGE,"E9"),sQuery(id+"F0.wireOp",EDGE,"E10"),sQuery(id+"F0.wireOp",EDGE,"E11"),sQuery(id+"F0.wireOp",EDGE,"E12"),sQuery(id+"F0.wireOp",EDGE,"E13"),sQuery(id+"F0.wireOp",EDGE,"E14"),sQuery(id+"F0.wireOp",EDGE,"E15")])],"isStart":false}),makeQuery(id+"F3.opExtrude","SWEPT_FACE",FACE,{"disambiguationData":[OSD([sQuery(id+"F2.wireOp",EDGE,"E37.left")])]})]}),makeQuery(id+"F5.opExtrude","SWEPT_FACE",FACE,{"disambiguationData":[OSD([sQuery(id+"F4.wireOp",EDGE,"E38.left")])]})]}),makeQuery(id+"F7.opExtrude","SWEPT_FACE",FACE,{"disambiguationData":[OSD([sQuery(id+"F6.wireOp",EDGE,"E39.left")])]})]}),makeQuery(id+"F9.opExtrude","SWEPT_FACE",FACE,{"disambiguationData":[OSD([sQuery(id+"F8.wireOp",EDGE,"E40.left")])]})]});
            var sketch = newSketch(context, id + "F54", { "sketchPlane" : qUnion([Q0])});
            skPoint(sketch, "E116", {"position": v(9.7, 45.3) * mm});
            skPoint(sketch, "E117", {"position": v(25.5, 45.36) * mm});
            skPoint(sketch, "E118", {"position": v(25.5, 4.64) * mm});
            skPoint(sketch, "E119", {"position": v(9.77, 4.64) * mm});
            skLineSegment(sketch, "E120", {"start": v(25.5, 4.64) * mm, "end": v(25.5, 45.36) * mm});
            skCircle(sketch, "E121", {"center": v(25.5, 25) * mm, "radius": 2.75 * mm});
            skPoint(sketch, "E122", {"position": v(25.5, 16) * mm});
            skPoint(sketch, "E123", {"position": v(25.5, 34) * mm});
            skCircle(sketch, "E124", {"center": v(25.5, 16) * mm, "radius": 2.25 * mm});
            skCircle(sketch, "E125", {"center": v(25.5, 34) * mm, "radius": 2.25 * mm});
            skLineSegment(sketch, "E126", {"start": v(9.77, 4.64) * mm, "end": v(9.7, 45.3) * mm});
            skPoint(sketch, "E127", {"position": v(9.74, 24.97) * mm});
            skCircle(sketch, "E128", {"center": v(9.74, 24.97) * mm, "radius": 1.75 * mm});
            skPoint(sketch, "E129", {"position": v(9.73, 33.97) * mm});
            skPoint(sketch, "E130", {"position": v(9.75, 15.97) * mm});
            skCircle(sketch, "E131", {"center": v(9.75, 15.97) * mm, "radius": 1.25 * mm});
            skCircle(sketch, "E132", {"center": v(9.73, 33.97) * mm, "radius": 1.25 * mm});
            skLineSegment(sketch, "E133", {"start": v(11.54, 45.3) * mm, "end": v(23.66, 45.36) * mm});
            skPoint(sketch, "E134", {"position": v(17.6, 45.33) * mm});
            skLineSegment(sketch, "E135", {"start": v(17.6, 45.33) * mm, "end": v(17.6, 36.33) * mm});
            skCircle(sketch, "E136", {"center": v(17.6, 36.33) * mm, "radius": 3.5 * mm});
            skSolve(sketch);
        }
        {
            var Q0;
            {var subQ0=sQuery(id+"F54.wireOp",EDGE,"3XNLnblx-CIP1-dcBc-11aQ-N01WHkB6yhVM");var subQ1=sQuery(id+"F54.wireOp",EDGE,"3p9cvuTi-4eDb-nzhx-HP4x-aUEWeS45vIfR");var subQ2=makeQuery(id+"F54.imprint","INTERSECT",VERTEX,{"disambiguationData":[OD(0.0)],"derivedFrom":[subQ1,subQ0]});Q0=makeQuery(id+"F54.imprint","IMPRINT",FACE,{"disambiguationData":[TD([[makeQuery(id+"F54.imprint","IMPRINT",EDGE,{"disambiguationData":[TD([[subQ2,-1.0]])],"derivedFrom":subQ1}),1.0]])]});}
            var Q1;
            {var subQ0=sQuery(id+"F54.wireOp",EDGE,"3XNLnblx-CIP1-dcBc-11aQ-N01WHkB6yhVM");var subQ1=sQuery(id+"F54.wireOp",EDGE,"3p9cvuTi-4eDb-nzhx-HP4x-aUEWeS45vIfR");var subQ2=makeQuery(id+"F54.imprint","INTERSECT",VERTEX,{"disambiguationData":[OD(0.0)],"derivedFrom":[subQ1,subQ0]});Q1=makeQuery(id+"F54.imprint","IMPRINT",FACE,{"disambiguationData":[TD([[makeQuery(id+"F54.imprint","IMPRINT",EDGE,{"disambiguationData":[TD([[subQ2,-1.0]])],"derivedFrom":subQ1}),-1.0]])]});}
            var Q2;
            {var subQ0=sQuery(id+"F54.wireOp",EDGE,"DDfOFf1o-U0pW-J5DL-B4GI-mtQAhWoh9h0L");var subQ1=sQuery(id+"F54.wireOp",EDGE,"E120");var subQ2=makeQuery(id+"F54.imprint","INTERSECT",VERTEX,{"disambiguationData":[OD(0.0)],"derivedFrom":[subQ1,subQ0]});Q2=makeQuery(id+"F54.imprint","IMPRINT",FACE,{"disambiguationData":[TD([[makeQuery(id+"F54.imprint","IMPRINT",EDGE,{"disambiguationData":[TD([[subQ2,-1.0]])],"derivedFrom":subQ1}),1.0]])]});}
            var Q3;
            {var subQ0=sQuery(id+"F54.wireOp",EDGE,"DDfOFf1o-U0pW-J5DL-B4GI-mtQAhWoh9h0L");var subQ1=sQuery(id+"F54.wireOp",EDGE,"E120");var subQ2=makeQuery(id+"F54.imprint","INTERSECT",VERTEX,{"disambiguationData":[OD(0.0)],"derivedFrom":[subQ1,subQ0]});Q3=makeQuery(id+"F54.imprint","IMPRINT",FACE,{"disambiguationData":[TD([[makeQuery(id+"F54.imprint","IMPRINT",EDGE,{"disambiguationData":[TD([[subQ2,-1.0]])],"derivedFrom":subQ1}),-1.0]])]});}
            var Q4;
            {var subQ0=sQuery(id+"F54.wireOp",EDGE,"E121");var subQ1=sQuery(id+"F54.wireOp",EDGE,"E120");var subQ2=makeQuery(id+"F54.imprint","INTERSECT",VERTEX,{"disambiguationData":[OD(0.0)],"derivedFrom":[subQ1,subQ0]});Q4=makeQuery(id+"F54.imprint","IMPRINT",FACE,{"disambiguationData":[TD([[makeQuery(id+"F54.imprint","IMPRINT",EDGE,{"disambiguationData":[TD([[subQ2,-1.0]])],"derivedFrom":subQ1}),-1.0]])]});}
            var Q5;
            {var subQ0=sQuery(id+"F54.wireOp",EDGE,"E121");var subQ1=sQuery(id+"F54.wireOp",EDGE,"E120");var subQ2=makeQuery(id+"F54.imprint","INTERSECT",VERTEX,{"disambiguationData":[OD(0.0)],"derivedFrom":[subQ1,subQ0]});Q5=makeQuery(id+"F54.imprint","IMPRINT",FACE,{"disambiguationData":[TD([[makeQuery(id+"F54.imprint","IMPRINT",EDGE,{"disambiguationData":[TD([[subQ2,-1.0]])],"derivedFrom":subQ1}),1.0]])]});}
            var Q6;
            {var subQ0=sQuery(id+"F54.wireOp",EDGE,"VWzquC7R-VlJN-Myvo-MNRv-5Y4p5CiWOKFd");var subQ1=sQuery(id+"F54.wireOp",EDGE,"E120");var subQ2=makeQuery(id+"F54.imprint","INTERSECT",VERTEX,{"disambiguationData":[OD(0.0)],"derivedFrom":[subQ1,subQ0]});Q6=makeQuery(id+"F54.imprint","IMPRINT",FACE,{"disambiguationData":[TD([[makeQuery(id+"F54.imprint","IMPRINT",EDGE,{"disambiguationData":[TD([[subQ2,-1.0]])],"derivedFrom":subQ1}),-1.0]])]});}
            var Q7;
            {var subQ0=sQuery(id+"F54.wireOp",EDGE,"VWzquC7R-VlJN-Myvo-MNRv-5Y4p5CiWOKFd");var subQ1=sQuery(id+"F54.wireOp",EDGE,"E120");var subQ2=makeQuery(id+"F54.imprint","INTERSECT",VERTEX,{"disambiguationData":[OD(0.0)],"derivedFrom":[subQ1,subQ0]});Q7=makeQuery(id+"F54.imprint","IMPRINT",FACE,{"disambiguationData":[TD([[makeQuery(id+"F54.imprint","IMPRINT",EDGE,{"disambiguationData":[TD([[subQ2,-1.0]])],"derivedFrom":subQ1}),1.0]])]});}
            var Q8;
            {var subQ0=sQuery(id+"F54.wireOp",EDGE,"Oqyc5hM3-dsuc-FuHj-EOHi-9WIJvw17gjAQ");var subQ1=sQuery(id+"F54.wireOp",EDGE,"3p9cvuTi-4eDb-nzhx-HP4x-aUEWeS45vIfR");var subQ2=makeQuery(id+"F54.imprint","INTERSECT",VERTEX,{"disambiguationData":[OD(0.0)],"derivedFrom":[subQ1,subQ0]});Q8=makeQuery(id+"F54.imprint","IMPRINT",FACE,{"disambiguationData":[TD([[makeQuery(id+"F54.imprint","IMPRINT",EDGE,{"disambiguationData":[TD([[subQ2,-1.0]])],"derivedFrom":subQ1}),-1.0]])]});}
            var Q9;
            {var subQ0=sQuery(id+"F54.wireOp",EDGE,"Oqyc5hM3-dsuc-FuHj-EOHi-9WIJvw17gjAQ");var subQ1=sQuery(id+"F54.wireOp",EDGE,"3p9cvuTi-4eDb-nzhx-HP4x-aUEWeS45vIfR");var subQ2=makeQuery(id+"F54.imprint","INTERSECT",VERTEX,{"disambiguationData":[OD(0.0)],"derivedFrom":[subQ1,subQ0]});Q9=makeQuery(id+"F54.imprint","IMPRINT",FACE,{"disambiguationData":[TD([[makeQuery(id+"F54.imprint","IMPRINT",EDGE,{"disambiguationData":[TD([[subQ2,-1.0]])],"derivedFrom":subQ1}),1.0]])]});}
            var Q10;
            {var subQ0=sQuery(id+"F54.wireOp",EDGE,"tojgxmme-YCLb-znB3-v4Q8-cUe67kHM2hgG");var subQ1=sQuery(id+"F54.wireOp",EDGE,"3p9cvuTi-4eDb-nzhx-HP4x-aUEWeS45vIfR");var subQ2=makeQuery(id+"F54.imprint","INTERSECT",VERTEX,{"disambiguationData":[OD(0.0)],"derivedFrom":[subQ1,subQ0]});Q10=makeQuery(id+"F54.imprint","IMPRINT",FACE,{"disambiguationData":[TD([[makeQuery(id+"F54.imprint","IMPRINT",EDGE,{"disambiguationData":[TD([[subQ2,-1.0]])],"derivedFrom":subQ1}),-1.0]])]});}
            var Q11;
            {var subQ0=sQuery(id+"F54.wireOp",EDGE,"tojgxmme-YCLb-znB3-v4Q8-cUe67kHM2hgG");var subQ1=sQuery(id+"F54.wireOp",EDGE,"3p9cvuTi-4eDb-nzhx-HP4x-aUEWeS45vIfR");var subQ2=makeQuery(id+"F54.imprint","INTERSECT",VERTEX,{"disambiguationData":[OD(0.0)],"derivedFrom":[subQ1,subQ0]});Q11=makeQuery(id+"F54.imprint","IMPRINT",FACE,{"disambiguationData":[TD([[makeQuery(id+"F54.imprint","IMPRINT",EDGE,{"disambiguationData":[TD([[subQ2,-1.0]])],"derivedFrom":subQ1}),1.0]])]});}
            extrude(context, id + "F55", {"entities" : qUnion([Q0, Q1, Q2, Q3, Q4, Q5, Q6, Q7, Q8, Q9, Q10, Q11]), "operationType" : NewBodyOperationType.REMOVE, "oppositeDirection" : true, "depth" : 25 * mm});
        }
        {
            var Q0;
            {var subQ0=sQuery(id+"F54.wireOp",EDGE,"E125");var subQ1=sQuery(id+"F54.wireOp",EDGE,"E120");var subQ2=makeQuery(id+"F54.imprint","INTERSECT",VERTEX,{"disambiguationData":[OD(0.0)],"derivedFrom":[subQ1,subQ0]});Q0=makeQuery(id+"F54.imprint","IMPRINT",FACE,{"disambiguationData":[TD([[makeQuery(id+"F54.imprint","IMPRINT",EDGE,{"disambiguationData":[TD([[subQ2,-1.0]])],"derivedFrom":subQ1}),1.0]])]});}
            var Q1;
            {var subQ0=sQuery(id+"F54.wireOp",EDGE,"E125");var subQ1=sQuery(id+"F54.wireOp",EDGE,"E120");var subQ2=makeQuery(id+"F54.imprint","INTERSECT",VERTEX,{"disambiguationData":[OD(0.0)],"derivedFrom":[subQ1,subQ0]});Q1=makeQuery(id+"F54.imprint","IMPRINT",FACE,{"disambiguationData":[TD([[makeQuery(id+"F54.imprint","IMPRINT",EDGE,{"disambiguationData":[TD([[subQ2,-1.0]])],"derivedFrom":subQ1}),-1.0]])]});}
            var Q2;
            {var subQ0=sQuery(id+"F54.wireOp",EDGE,"E124");var subQ1=sQuery(id+"F54.wireOp",EDGE,"E120");var subQ2=makeQuery(id+"F54.imprint","INTERSECT",VERTEX,{"disambiguationData":[OD(0.0)],"derivedFrom":[subQ1,subQ0]});Q2=makeQuery(id+"F54.imprint","IMPRINT",FACE,{"disambiguationData":[TD([[makeQuery(id+"F54.imprint","IMPRINT",EDGE,{"disambiguationData":[TD([[subQ2,-1.0]])],"derivedFrom":subQ1}),1.0]])]});}
            var Q3;
            {var subQ0=sQuery(id+"F54.wireOp",EDGE,"E124");var subQ1=sQuery(id+"F54.wireOp",EDGE,"E120");var subQ2=makeQuery(id+"F54.imprint","INTERSECT",VERTEX,{"disambiguationData":[OD(0.0)],"derivedFrom":[subQ1,subQ0]});Q3=makeQuery(id+"F54.imprint","IMPRINT",FACE,{"disambiguationData":[TD([[makeQuery(id+"F54.imprint","IMPRINT",EDGE,{"disambiguationData":[TD([[subQ2,-1.0]])],"derivedFrom":subQ1}),-1.0]])]});}
            extrude(context, id + "F56", {"entities" : qUnion([Q0, Q1, Q2, Q3]), "operationType" : NewBodyOperationType.REMOVE, "oppositeDirection" : true, "depth" : 25 * mm, "offsetDistance" : 25 * mm});
        }
        {
            var Q0;
            Q0 = qSketchRegion(id + "F54", true);
            extrude(context, id + "F57", {"entities" : qUnion([Q0]), "operationType" : NewBodyOperationType.REMOVE, "oppositeDirection" : true, "depth" : 25 * mm, "offsetDistance" : 25 * mm});
        }
        {
            var Q0;
            Q0=makeQuery(id+"F50.opExtrude","CAP_EDGE",EDGE,{"disambiguationData":[OSD([sQuery(id+"F49.wireOp",EDGE,"E110.bottom")])],"isStart":false});
            var Q1;
            Q1=makeQuery(id+"F46.opExtrude","CAP_EDGE",EDGE,{"disambiguationData":[OSD([sQuery(id+"F45.wireOp",EDGE,"E104.top")])],"isStart":false});
            fillet(context, id + "F58", {"entities" : qUnion([Q0, Q1]), "radius" : 7 * mm, "tangentPropagation" : true, "allowEdgeOverflow" : false});
        }
    });
